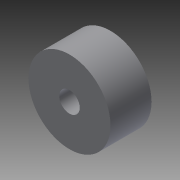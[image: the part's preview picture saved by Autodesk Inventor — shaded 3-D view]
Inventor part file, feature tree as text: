
AUTODESK INVENTOR PART (.ipt)
format: ipt  version: 2013 (Build 170138000, 138)  size: 81,408 bytes
history: native  units: in
note: dims shown in document units (in); Inventor stores cm internally (conversion verified against a paired STEP export)
features: extrude x2, sketch x2
ambient origin geometry x8: Origin, YZ Plane, XZ Plane, XY Plane, X Axis, Y Axis, Z Axis, Center Point
bodies: Solid1 (feature_tree)
feature tree (4):
  extrude  "Extrusion1"  Depth=0.375in TaperAngle=0.0deg
  extrude  "Extrusion2"  Depth=1.0in TaperAngle=0.0deg
  sketch  "Sketch1"  dims[d0=0.75in d1=0.375in d2=0.0in]
  sketch  "Sketch2"  dims[d3=0.1875in d4=1.0in d5=0.0in]
